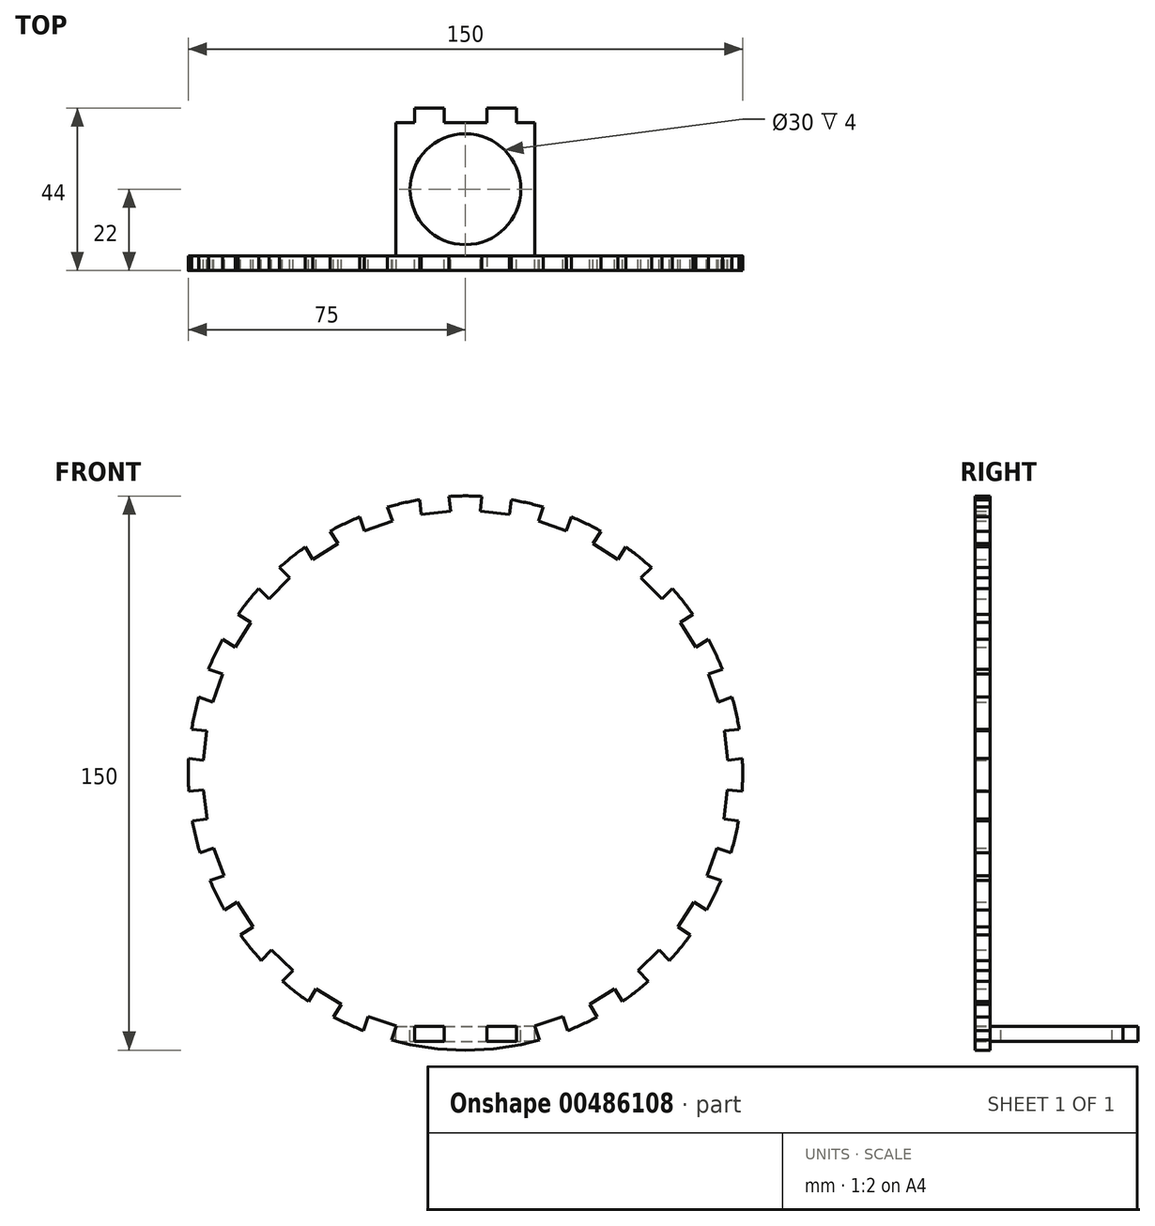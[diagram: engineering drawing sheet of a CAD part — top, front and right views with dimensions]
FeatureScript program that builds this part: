
annotation { "Feature Type Name" : "Feature", "Feature Type Description" : "" }
export const myFeature = defineFeature(function(context is Context, id is Id, definition is map)
    precondition{}
    {
        {
            var Q0;
            Q0=qCreatedBy(makeId("Front.planeOp"),FACE);
            var sketch = newSketch(context, id + "F0", { "sketchPlane" : qUnion([Q0])});
            skArc(sketch, "E0", {"start": v(-20.01, -72.28) * mm, "mid": v(0, -75) * mm, "end": v(20.01, -72.28) * mm});
            skLineSegment(sketch, "E1.bottom", {"start": v(-13.78, -68.61) * mm, "end": v(-5.78, -68.61) * mm});
            skLineSegment(sketch, "E1.top", {"start": v(-13.78, -72.61) * mm, "end": v(-5.78, -72.61) * mm});
            skLineSegment(sketch, "E1.left", {"start": v(-18.78, -68.61) * mm, "end": v(-18.78, -72.61) * mm, "construction": true});
            skLineSegment(sketch, "E1.right", {"start": v(18.78, -68.61) * mm, "end": v(18.78, -72.61) * mm, "construction": true});
            skLineSegment(sketch, "E2", {"start": v(-26.32, -65.95) * mm, "end": v(-27.6, -69.74) * mm});
            skLineSegment(sketch, "E3", {"start": v(-26.32, -65.95) * mm, "end": v(-18.74, -68.49) * mm});
            skLineSegment(sketch, "E4", {"start": v(-18.74, -68.49) * mm, "end": v(-20.01, -72.28) * mm});
            skLineSegment(sketch, "E5", {"start": v(-33.58, -62.57) * mm, "end": v(-26.32, -65.95) * mm, "construction": true});
            skLineSegment(sketch, "E6", {"start": v(-40.4, -58.4) * mm, "end": v(-42.49, -61.8) * mm});
            skLineSegment(sketch, "E7", {"start": v(-40.4, -58.4) * mm, "end": v(-33.58, -62.57) * mm});
            skLineSegment(sketch, "E8", {"start": v(-33.58, -62.57) * mm, "end": v(-35.66, -65.98) * mm});
            skLineSegment(sketch, "E9", {"start": v(-52.43, -47.88) * mm, "end": v(-55.23, -50.74) * mm});
            skLineSegment(sketch, "E10", {"start": v(-52.43, -47.88) * mm, "end": v(-46.71, -53.48) * mm});
            skLineSegment(sketch, "E11", {"start": v(-46.71, -53.48) * mm, "end": v(-49.5, -56.34) * mm});
            skLineSegment(sketch, "E12", {"start": v(-57.48, -41.68) * mm, "end": v(-52.43, -47.88) * mm, "construction": true});
            skLineSegment(sketch, "E13", {"start": v(-61.8, -34.95) * mm, "end": v(-65.17, -37.11) * mm});
            skLineSegment(sketch, "E14", {"start": v(-61.8, -34.95) * mm, "end": v(-57.48, -41.68) * mm});
            skLineSegment(sketch, "E15", {"start": v(-57.48, -41.68) * mm, "end": v(-60.85, -43.84) * mm});
            skLineSegment(sketch, "E16", {"start": v(-46.71, -53.48) * mm, "end": v(-40.4, -58.4) * mm, "construction": true});
            skLineSegment(sketch, "E17", {"start": v(-68.06, -20.25) * mm, "end": v(-71.82, -21.6) * mm});
            skLineSegment(sketch, "E18", {"start": v(-68.06, -20.25) * mm, "end": v(-65.35, -27.78) * mm});
            skLineSegment(sketch, "E19", {"start": v(-65.35, -27.78) * mm, "end": v(-69.11, -29.13) * mm});
            skLineSegment(sketch, "E20", {"start": v(-69.9, -12.46) * mm, "end": v(-68.06, -20.25) * mm, "construction": true});
            skLineSegment(sketch, "E21", {"start": v(-70.86, -4.52) * mm, "end": v(-74.83, -5) * mm});
            skLineSegment(sketch, "E22", {"start": v(-70.86, -4.52) * mm, "end": v(-69.9, -12.46) * mm});
            skLineSegment(sketch, "E23", {"start": v(-69.9, -12.46) * mm, "end": v(-73.87, -12.94) * mm});
            skLineSegment(sketch, "E24", {"start": v(-70.08, 11.43) * mm, "end": v(-74.06, 11.85) * mm});
            skLineSegment(sketch, "E25", {"start": v(-70.08, 11.43) * mm, "end": v(-70.92, 3.48) * mm});
            skLineSegment(sketch, "E26", {"start": v(-70.92, 3.48) * mm, "end": v(-74.9, 3.9) * mm});
            skLineSegment(sketch, "E27", {"start": v(-68.35, 19.24) * mm, "end": v(-70.08, 11.43) * mm, "construction": true});
            skLineSegment(sketch, "E28", {"start": v(-65.75, 26.8) * mm, "end": v(-69.53, 28.1) * mm});
            skLineSegment(sketch, "E29", {"start": v(-65.75, 26.8) * mm, "end": v(-68.35, 19.24) * mm});
            skLineSegment(sketch, "E30", {"start": v(-68.35, 19.24) * mm, "end": v(-72.13, 20.54) * mm});
            skLineSegment(sketch, "E31", {"start": v(-70.92, 3.48) * mm, "end": v(-70.86, -4.52) * mm, "construction": true});
            skLineSegment(sketch, "E32", {"start": v(-65.35, -27.78) * mm, "end": v(-61.8, -34.95) * mm, "construction": true});
            skLineSegment(sketch, "E33", {"start": v(-58.1, 40.83) * mm, "end": v(-61.49, 42.94) * mm});
            skLineSegment(sketch, "E34", {"start": v(-58.1, 40.83) * mm, "end": v(-62.32, 34.04) * mm});
            skLineSegment(sketch, "E35", {"start": v(-62.32, 34.04) * mm, "end": v(-65.71, 36.15) * mm});
            skLineSegment(sketch, "E36", {"start": v(-53.13, 47.1) * mm, "end": v(-58.1, 40.83) * mm, "construction": true});
            skLineSegment(sketch, "E37", {"start": v(-47.5, 52.78) * mm, "end": v(-50.33, 55.6) * mm});
            skLineSegment(sketch, "E38", {"start": v(-47.5, 52.78) * mm, "end": v(-53.13, 47.1) * mm});
            skLineSegment(sketch, "E39", {"start": v(-53.13, 47.1) * mm, "end": v(-55.97, 49.92) * mm});
            skLineSegment(sketch, "E40", {"start": v(-34.5, 62.06) * mm, "end": v(-36.63, 65.45) * mm});
            skLineSegment(sketch, "E41", {"start": v(-34.5, 62.06) * mm, "end": v(-41.26, 57.8) * mm});
            skLineSegment(sketch, "E42", {"start": v(-41.26, 57.8) * mm, "end": v(-43.4, 61.17) * mm});
            skLineSegment(sketch, "E43", {"start": v(-27.3, 65.55) * mm, "end": v(-34.5, 62.06) * mm, "construction": true});
            skLineSegment(sketch, "E44", {"start": v(-19.75, 68.2) * mm, "end": v(-21.07, 71.98) * mm});
            skLineSegment(sketch, "E45", {"start": v(-19.75, 68.2) * mm, "end": v(-27.3, 65.55) * mm});
            skLineSegment(sketch, "E46", {"start": v(-27.3, 65.55) * mm, "end": v(-28.62, 69.32) * mm});
            skLineSegment(sketch, "E47", {"start": v(-41.26, 57.8) * mm, "end": v(-47.5, 52.78) * mm, "construction": true});
            skLineSegment(sketch, "E48", {"start": v(-65.75, 26.8) * mm, "end": v(-62.32, 34.04) * mm, "construction": true});
            skLineSegment(sketch, "E49", {"start": v(-4, 70.9) * mm, "end": v(-4.45, 74.87) * mm});
            skLineSegment(sketch, "E50", {"start": v(-4, 70.9) * mm, "end": v(-11.95, 70) * mm});
            skLineSegment(sketch, "E51", {"start": v(-11.95, 70) * mm, "end": v(-12.4, 73.97) * mm});
            skLineSegment(sketch, "E52", {"start": v(4, 70.9) * mm, "end": v(-4, 70.9) * mm, "construction": true});
            skLineSegment(sketch, "E53", {"start": v(11.95, 70) * mm, "end": v(12.4, 73.97) * mm});
            skLineSegment(sketch, "E54", {"start": v(11.95, 70) * mm, "end": v(4, 70.9) * mm});
            skLineSegment(sketch, "E55", {"start": v(4, 70.9) * mm, "end": v(4.45, 74.87) * mm});
            skLineSegment(sketch, "E56", {"start": v(27.3, 65.55) * mm, "end": v(28.62, 69.32) * mm});
            skLineSegment(sketch, "E57", {"start": v(27.3, 65.55) * mm, "end": v(19.75, 68.2) * mm});
            skLineSegment(sketch, "E58", {"start": v(19.75, 68.2) * mm, "end": v(21.07, 71.98) * mm});
            skLineSegment(sketch, "E59", {"start": v(34.5, 62.06) * mm, "end": v(27.3, 65.55) * mm, "construction": true});
            skLineSegment(sketch, "E60", {"start": v(41.26, 57.8) * mm, "end": v(43.4, 61.17) * mm});
            skLineSegment(sketch, "E61", {"start": v(41.26, 57.8) * mm, "end": v(34.5, 62.06) * mm});
            skLineSegment(sketch, "E62", {"start": v(34.5, 62.06) * mm, "end": v(36.63, 65.45) * mm});
            skLineSegment(sketch, "E63", {"start": v(19.75, 68.2) * mm, "end": v(11.95, 70) * mm, "construction": true});
            skLineSegment(sketch, "E64", {"start": v(53.13, 47.1) * mm, "end": v(55.97, 49.92) * mm});
            skLineSegment(sketch, "E65", {"start": v(53.13, 47.1) * mm, "end": v(47.5, 52.78) * mm});
            skLineSegment(sketch, "E66", {"start": v(47.5, 52.78) * mm, "end": v(50.33, 55.6) * mm});
            skLineSegment(sketch, "E67", {"start": v(58.1, 40.83) * mm, "end": v(53.13, 47.1) * mm, "construction": true});
            skLineSegment(sketch, "E68", {"start": v(62.32, 34.04) * mm, "end": v(65.71, 36.15) * mm});
            skLineSegment(sketch, "E69", {"start": v(62.32, 34.04) * mm, "end": v(58.1, 40.83) * mm});
            skLineSegment(sketch, "E70", {"start": v(58.1, 40.83) * mm, "end": v(61.49, 42.94) * mm});
            skLineSegment(sketch, "E71", {"start": v(68.35, 19.24) * mm, "end": v(72.13, 20.54) * mm});
            skLineSegment(sketch, "E72", {"start": v(68.35, 19.24) * mm, "end": v(65.75, 26.8) * mm});
            skLineSegment(sketch, "E73", {"start": v(65.75, 26.8) * mm, "end": v(69.53, 28.1) * mm});
            skLineSegment(sketch, "E74", {"start": v(70.08, 11.43) * mm, "end": v(68.35, 19.24) * mm, "construction": true});
            skLineSegment(sketch, "E75", {"start": v(70.92, 3.48) * mm, "end": v(74.9, 3.9) * mm});
            skLineSegment(sketch, "E76", {"start": v(70.92, 3.48) * mm, "end": v(70.08, 11.43) * mm});
            skLineSegment(sketch, "E77", {"start": v(70.08, 11.43) * mm, "end": v(74.06, 11.85) * mm});
            skLineSegment(sketch, "E78", {"start": v(65.75, 26.8) * mm, "end": v(62.32, 34.04) * mm, "construction": true});
            skLineSegment(sketch, "E79", {"start": v(69.9, -12.46) * mm, "end": v(73.87, -12.94) * mm});
            skLineSegment(sketch, "E80", {"start": v(69.9, -12.46) * mm, "end": v(70.86, -4.52) * mm});
            skLineSegment(sketch, "E81", {"start": v(70.86, -4.52) * mm, "end": v(74.83, -5) * mm});
            skLineSegment(sketch, "E82", {"start": v(68.06, -20.25) * mm, "end": v(69.9, -12.46) * mm, "construction": true});
            skLineSegment(sketch, "E83", {"start": v(65.35, -27.78) * mm, "end": v(69.11, -29.13) * mm});
            skLineSegment(sketch, "E84", {"start": v(65.35, -27.78) * mm, "end": v(68.06, -20.25) * mm});
            skLineSegment(sketch, "E85", {"start": v(68.06, -20.25) * mm, "end": v(71.82, -21.6) * mm});
            skLineSegment(sketch, "E86", {"start": v(57.48, -41.68) * mm, "end": v(60.85, -43.84) * mm});
            skLineSegment(sketch, "E87", {"start": v(57.48, -41.68) * mm, "end": v(61.8, -34.95) * mm});
            skLineSegment(sketch, "E88", {"start": v(61.8, -34.95) * mm, "end": v(65.17, -37.11) * mm});
            skLineSegment(sketch, "E89", {"start": v(52.43, -47.88) * mm, "end": v(57.48, -41.68) * mm, "construction": true});
            skLineSegment(sketch, "E90", {"start": v(46.71, -53.48) * mm, "end": v(49.5, -56.34) * mm});
            skLineSegment(sketch, "E91", {"start": v(46.71, -53.48) * mm, "end": v(52.43, -47.88) * mm});
            skLineSegment(sketch, "E92", {"start": v(52.43, -47.88) * mm, "end": v(55.23, -50.74) * mm});
            skLineSegment(sketch, "E93", {"start": v(61.8, -34.95) * mm, "end": v(65.35, -27.78) * mm, "construction": true});
            skLineSegment(sketch, "E94", {"start": v(-19.75, 68.2) * mm, "end": v(-11.95, 70) * mm, "construction": true});
            skLineSegment(sketch, "E95", {"start": v(41.26, 57.8) * mm, "end": v(47.5, 52.78) * mm, "construction": true});
            skLineSegment(sketch, "E96", {"start": v(70.92, 3.48) * mm, "end": v(70.86, -4.52) * mm, "construction": true});
            skLineSegment(sketch, "E97", {"start": v(46.71, -53.48) * mm, "end": v(40.4, -58.4) * mm, "construction": true});
            skLineSegment(sketch, "E98", {"start": v(33.58, -62.57) * mm, "end": v(35.66, -65.98) * mm});
            skLineSegment(sketch, "E99", {"start": v(40.4, -58.4) * mm, "end": v(42.49, -61.8) * mm});
            skLineSegment(sketch, "E100", {"start": v(40.4, -58.4) * mm, "end": v(33.58, -62.57) * mm});
            skLineSegment(sketch, "E101", {"start": v(33.58, -62.57) * mm, "end": v(26.32, -65.95) * mm, "construction": true});
            skLineSegment(sketch, "E102", {"start": v(26.32, -65.95) * mm, "end": v(18.74, -68.49) * mm});
            skLineSegment(sketch, "E103", {"start": v(18.74, -68.49) * mm, "end": v(20.01, -72.28) * mm});
            skLineSegment(sketch, "E104", {"start": v(26.32, -65.95) * mm, "end": v(27.6, -69.74) * mm});
            skLineSegment(sketch, "E105", {"start": v(-13.78, -68.61) * mm, "end": v(-13.78, -72.61) * mm});
            skLineSegment(sketch, "E106", {"start": v(13.78, -68.61) * mm, "end": v(13.78, -72.61) * mm});
            skLineSegment(sketch, "E107", {"start": v(-5.78, -68.61) * mm, "end": v(-5.78, -72.61) * mm});
            skLineSegment(sketch, "E108", {"start": v(5.78, -68.61) * mm, "end": v(5.78, -72.61) * mm});
            skLineSegment(sketch, "E109.trimOffspring", {"start": v(5.78, -72.61) * mm, "end": v(13.78, -72.61) * mm});
            skLineSegment(sketch, "E110.trimOffspring", {"start": v(5.78, -68.61) * mm, "end": v(13.78, -68.61) * mm});
            skArc(sketch, "E111.trimOffspring", {"start": v(-35.66, -65.98) * mm, "mid": v(-31.68, -67.98) * mm, "end": v(-27.6, -69.74) * mm});
            skArc(sketch, "E112.trimOffspring", {"start": v(-49.5, -56.34) * mm, "mid": v(-46.08, -59.18) * mm, "end": v(-42.49, -61.8) * mm});
            skArc(sketch, "E113.trimOffspring", {"start": v(-60.85, -43.84) * mm, "mid": v(-58.14, -47.38) * mm, "end": v(-55.23, -50.74) * mm});
            skArc(sketch, "E114.trimOffspring", {"start": v(-69.11, -29.13) * mm, "mid": v(-67.26, -33.18) * mm, "end": v(-65.17, -37.11) * mm});
            skArc(sketch, "E115.trimOffspring", {"start": v(-73.87, -12.94) * mm, "mid": v(-72.98, -17.3) * mm, "end": v(-71.82, -21.6) * mm});
            skArc(sketch, "E116.trimOffspring", {"start": v(-74.9, 3.9) * mm, "mid": v(-75, -0.55) * mm, "end": v(-74.83, -5) * mm});
            skArc(sketch, "E117.trimOffspring", {"start": v(-72.13, 20.54) * mm, "mid": v(-73.22, 16.23) * mm, "end": v(-74.06, 11.85) * mm});
            skArc(sketch, "E118.trimOffspring", {"start": v(-65.71, 36.15) * mm, "mid": v(-67.74, 32.19) * mm, "end": v(-69.53, 28.1) * mm});
            skArc(sketch, "E119.trimOffspring", {"start": v(-55.97, 49.92) * mm, "mid": v(-58.83, 46.51) * mm, "end": v(-61.49, 42.94) * mm});
            skArc(sketch, "E120.trimOffspring", {"start": v(-43.4, 61.17) * mm, "mid": v(-46.95, 58.49) * mm, "end": v(-50.33, 55.6) * mm});
            skArc(sketch, "E121.trimOffspring", {"start": v(-28.62, 69.32) * mm, "mid": v(-32.68, 67.5) * mm, "end": v(-36.63, 65.45) * mm});
            skArc(sketch, "E122.trimOffspring", {"start": v(-12.4, 73.97) * mm, "mid": v(-16.77, 73.1) * mm, "end": v(-21.07, 71.98) * mm});
            skArc(sketch, "E123.trimOffspring", {"start": v(4.45, 74.87) * mm, "mid": v(0, 75) * mm, "end": v(-4.45, 74.87) * mm});
            skArc(sketch, "E124.trimOffspring", {"start": v(21.07, 71.98) * mm, "mid": v(16.77, 73.1) * mm, "end": v(12.4, 73.97) * mm});
            skArc(sketch, "E125.trimOffspring", {"start": v(36.63, 65.45) * mm, "mid": v(32.68, 67.5) * mm, "end": v(28.62, 69.32) * mm});
            skArc(sketch, "E126.trimOffspring", {"start": v(50.33, 55.6) * mm, "mid": v(46.95, 58.49) * mm, "end": v(43.4, 61.17) * mm});
            skArc(sketch, "E127.trimOffspring", {"start": v(61.49, 42.94) * mm, "mid": v(58.83, 46.51) * mm, "end": v(55.97, 49.92) * mm});
            skArc(sketch, "E128.trimOffspring", {"start": v(69.53, 28.1) * mm, "mid": v(67.74, 32.19) * mm, "end": v(65.71, 36.15) * mm});
            skArc(sketch, "E129.trimOffspring", {"start": v(74.06, 11.85) * mm, "mid": v(73.22, 16.23) * mm, "end": v(72.13, 20.54) * mm});
            skArc(sketch, "E130.trimOffspring", {"start": v(74.83, -5) * mm, "mid": v(75, -0.55) * mm, "end": v(74.9, 3.9) * mm});
            skArc(sketch, "E131.trimOffspring", {"start": v(71.82, -21.6) * mm, "mid": v(72.98, -17.3) * mm, "end": v(73.87, -12.94) * mm});
            skArc(sketch, "E132.trimOffspring", {"start": v(65.17, -37.11) * mm, "mid": v(67.26, -33.18) * mm, "end": v(69.11, -29.13) * mm});
            skArc(sketch, "E133.trimOffspring", {"start": v(55.23, -50.74) * mm, "mid": v(58.14, -47.38) * mm, "end": v(60.85, -43.84) * mm});
            skArc(sketch, "E134.trimOffspring", {"start": v(42.49, -61.8) * mm, "mid": v(46.08, -59.18) * mm, "end": v(49.5, -56.34) * mm});
            skArc(sketch, "E135.trimOffspring", {"start": v(27.6, -69.74) * mm, "mid": v(31.68, -67.98) * mm, "end": v(35.66, -65.98) * mm});
            skSolve(sketch);
        }
        {
            var Q0;
            Q0 = qSketchRegion(id + "F0", true);
            extrude(context, id + "F1", {"entities" : qUnion([Q0]), "depth" : 4 * mm});
        }
        {
            var Q0;
            Q0=makeQuery(id+"F1.opExtrude","SWEPT_FACE",FACE,{"disambiguationData":[OSD([sQuery(id+"F0.wireOp",EDGE,"E1.bottom")])]});
            var sketch = newSketch(context, id + "F2", { "sketchPlane" : qUnion([Q0])});
            skLineSegment(sketch, "E136", {"start": v(-5.78, 0) * mm, "end": v(-5.78, 4) * mm});
            skLineSegment(sketch, "E137", {"start": v(-5.78, 4) * mm, "end": v(-13.78, 4) * mm});
            skLineSegment(sketch, "E138", {"start": v(-13.78, 4) * mm, "end": v(-13.78, 0) * mm});
            skLineSegment(sketch, "E139", {"start": v(-13.78, 0) * mm, "end": v(-18.78, 0) * mm});
            skLineSegment(sketch, "E140", {"start": v(-5.78, 0) * mm, "end": v(5.78, 0) * mm});
            skLineSegment(sketch, "E141", {"start": v(5.78, 0) * mm, "end": v(5.78, 4) * mm});
            skLineSegment(sketch, "E142", {"start": v(5.78, 4) * mm, "end": v(13.78, 4) * mm});
            skLineSegment(sketch, "E143", {"start": v(13.78, 4) * mm, "end": v(13.78, 0) * mm});
            skLineSegment(sketch, "E144", {"start": v(13.78, 0) * mm, "end": v(18.78, 0) * mm});
            skLineSegment(sketch, "E145", {"start": v(-18.78, 0) * mm, "end": v(-18.78, -36) * mm});
            skLineSegment(sketch, "E146", {"start": v(18.78, 0) * mm, "end": v(18.78, -36) * mm});
            skLineSegment(sketch, "E147", {"start": v(18.78, -36) * mm, "end": v(13.78, -36) * mm});
            skLineSegment(sketch, "E148", {"start": v(13.78, -36) * mm, "end": v(13.78, -40) * mm});
            skPoint(sketch, "E148.endSnap0", {"position": v(13.78, 2) * mm});
            skLineSegment(sketch, "E149", {"start": v(13.78, -40) * mm, "end": v(5.78, -40) * mm});
            skLineSegment(sketch, "E150", {"start": v(5.78, -40) * mm, "end": v(5.78, -36) * mm});
            skLineSegment(sketch, "E151", {"start": v(5.78, -36) * mm, "end": v(-5.78, -36) * mm});
            skLineSegment(sketch, "E152", {"start": v(-5.78, -36) * mm, "end": v(-5.78, -40) * mm});
            skLineSegment(sketch, "E153", {"start": v(-5.78, -40) * mm, "end": v(-13.78, -40) * mm});
            skLineSegment(sketch, "E154", {"start": v(-13.78, -40) * mm, "end": v(-13.78, -36) * mm});
            skLineSegment(sketch, "E155", {"start": v(-13.78, -36) * mm, "end": v(-18.78, -36) * mm});
            skLineSegment(sketch, "E156", {"start": v(0, 0) * mm, "end": v(0, -36) * mm, "construction": true});
            skCircle(sketch, "E157", {"center": v(0, -18) * mm, "radius": 15 * mm});
            skSolve(sketch);
        }
        {
            var Q0;
            Q0=makeQuery(id+"F2.imprint","IMPRINT",FACE,{"disambiguationData":[TD([[makeQuery(id+"F2.imprint","IMPRINT",EDGE,{"derivedFrom":sQuery(id+"F2.wireOp",EDGE,"E139")}),1.0]])]});
            extrude(context, id + "F3", {"entities" : qUnion([Q0]), "depth" : 4 * mm});
        }
    });
